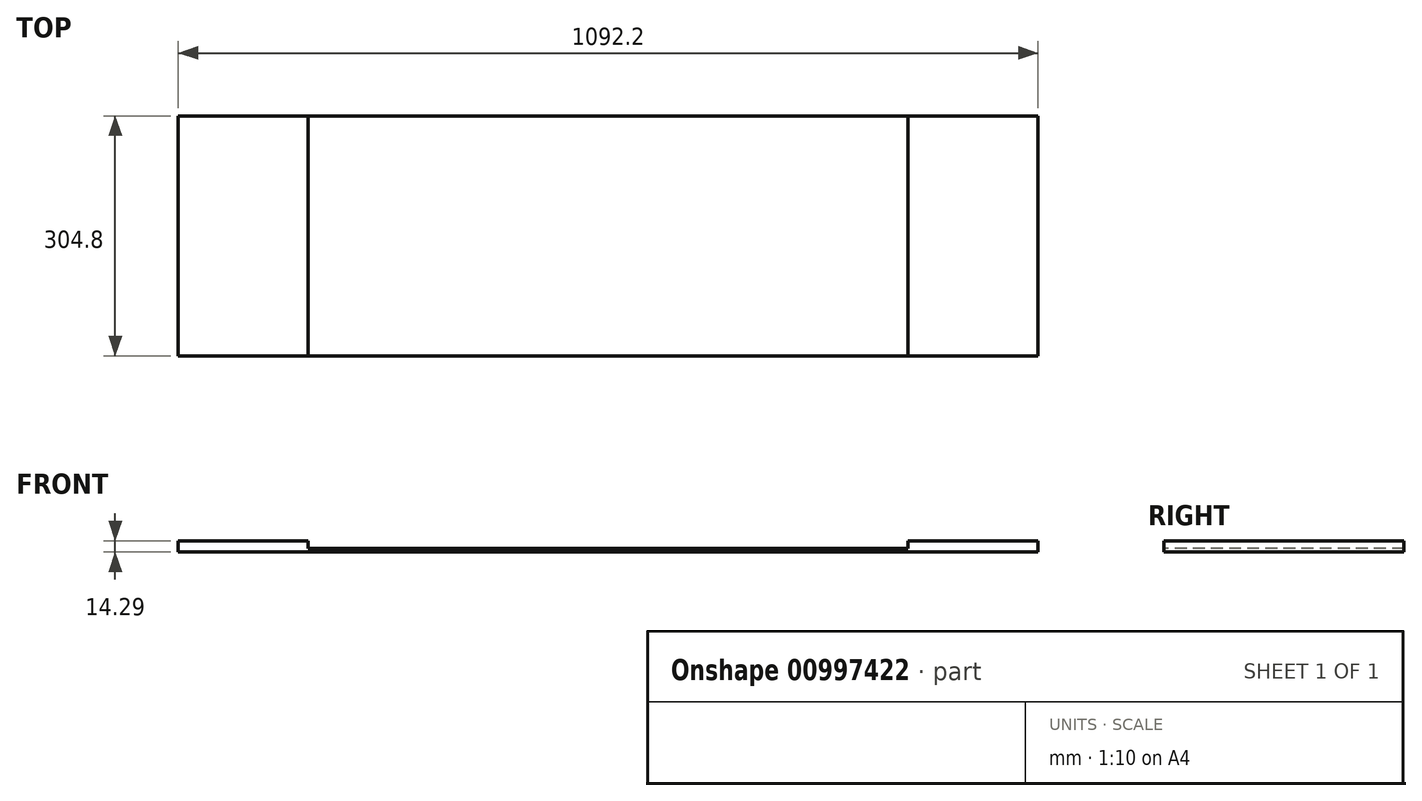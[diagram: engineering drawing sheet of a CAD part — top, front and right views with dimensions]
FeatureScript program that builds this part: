
annotation { "Feature Type Name" : "Feature", "Feature Type Description" : "" }
export const myFeature = defineFeature(function(context is Context, id is Id, definition is map)
    precondition{}
    {
        {
            var Q0;
            Q0=qCreatedBy(makeId("Top.planeOp"),FACE);
            var sketch = newSketch(context, id + "F0", { "sketchPlane" : qUnion([Q0])});
            skLineSegment(sketch, "E0.bottom", {"start": v(-42.8, 257.99) * mm, "end": v(1049.4, 257.99) * mm});
            skLineSegment(sketch, "E0.top", {"start": v(-42.8, -46.81) * mm, "end": v(1049.4, -46.81) * mm});
            skLineSegment(sketch, "E0.left", {"start": v(-42.8, 257.99) * mm, "end": v(-42.8, -46.81) * mm});
            skLineSegment(sketch, "E0.right", {"start": v(1049.4, 257.99) * mm, "end": v(1049.4, -46.81) * mm});
            skSolve(sketch);
        }
        {
            var Q0;
            Q0 = qSketchRegion(id + "F0", true);
            extrude(context, id + "F1", {"entities" : qUnion([Q0]), "depth" : 4.76 * mm, "offsetDistance" : 25.4 * mm});
        }
        {
            var Q0;
            Q0=makeQuery(id+"F1.opExtrude","CAP_FACE",FACE,{"disambiguationData":[OSD([sQuery(id+"F0.wireOp",EDGE,"E0.bottom"),sQuery(id+"F0.wireOp",EDGE,"E0.top"),sQuery(id+"F0.wireOp",EDGE,"E0.left"),sQuery(id+"F0.wireOp",EDGE,"E0.right")])],"isStart":false});
            var sketch = newSketch(context, id + "F2", { "sketchPlane" : qUnion([Q0])});
            skLineSegment(sketch, "E1.left", {"start": v(122.3, 257.99) * mm, "end": v(122.3, -46.81) * mm});
            skLineSegment(sketch, "E1.right", {"start": v(884.3, 257.99) * mm, "end": v(884.3, -46.81) * mm});
            skLineSegment(sketch, "E2.bottom", {"start": v(-42.8, 257.99) * mm, "end": v(122.3, 257.99) * mm});
            skLineSegment(sketch, "E2.top", {"start": v(-42.8, -46.81) * mm, "end": v(122.3, -46.81) * mm});
            skLineSegment(sketch, "E2.left", {"start": v(-42.8, 257.99) * mm, "end": v(-42.8, -46.81) * mm});
            skLineSegment(sketch, "E3.bottom", {"start": v(884.3, -46.81) * mm, "end": v(1049.4, -46.81) * mm});
            skLineSegment(sketch, "E3.top", {"start": v(884.3, 257.99) * mm, "end": v(1049.4, 257.99) * mm});
            skLineSegment(sketch, "E3.left", {"start": v(884.3, -46.81) * mm, "end": v(884.3, 257.99) * mm});
            skLineSegment(sketch, "E3.right", {"start": v(1049.4, -46.81) * mm, "end": v(1049.4, 257.99) * mm});
            skSolve(sketch);
        }
        {
            var Q0;
            Q0 = qSketchRegion(id + "F2", true);
            extrude(context, id + "F3", {"entities" : qUnion([Q0]), "operationType" : NewBodyOperationType.ADD, "depth" : 9.52 * mm, "offsetDistance" : 25.4 * mm});
        }
    });
